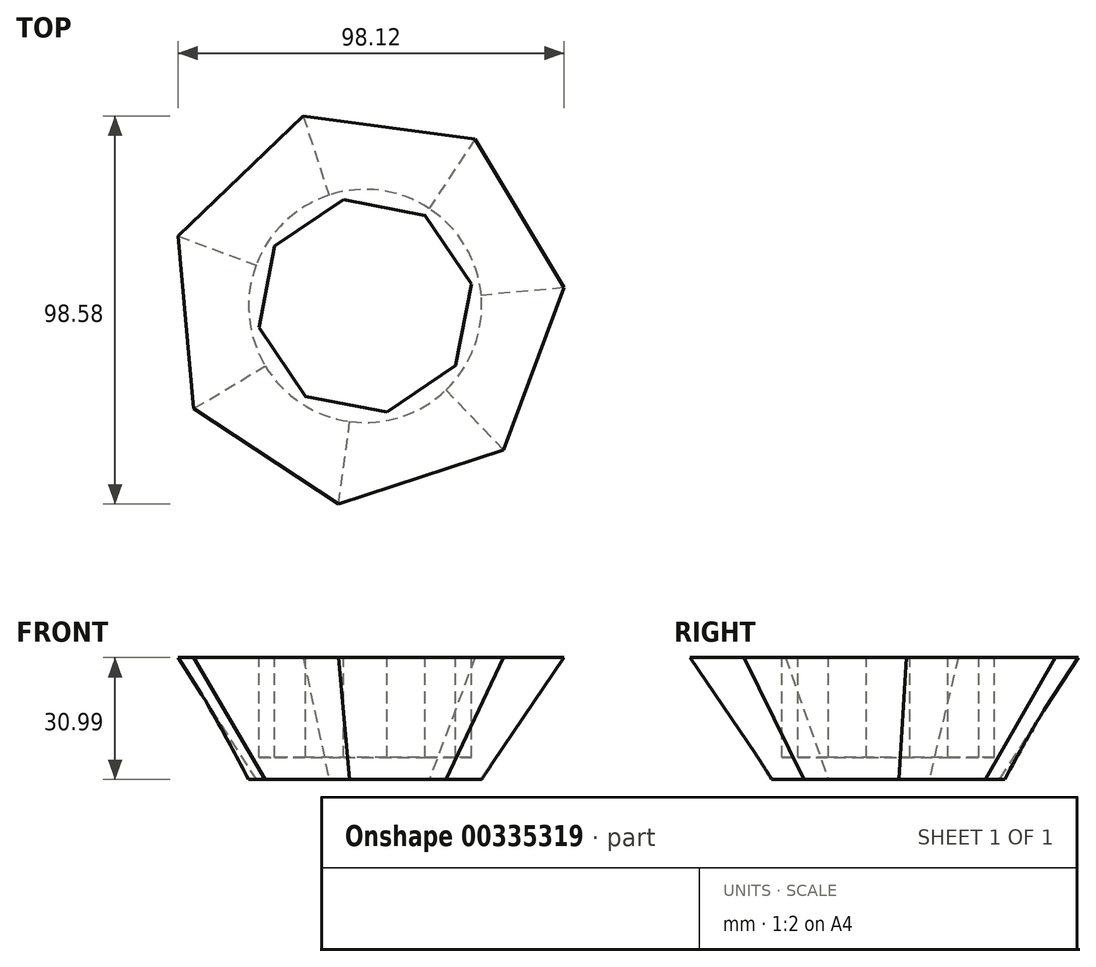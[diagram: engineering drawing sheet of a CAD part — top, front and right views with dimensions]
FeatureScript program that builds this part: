
annotation { "Feature Type Name" : "Feature", "Feature Type Description" : "" }
export const myFeature = defineFeature(function(context is Context, id is Id, definition is map)
    precondition{}
    {
        {
            var Q0;
            Q0=qCreatedBy(makeId("Top.planeOp"),FACE);
            var sketch = newSketch(context, id + "F0", { "sketchPlane" : qUnion([Q0])});
            skCircle(sketch, "E0", {"center": v(0, 0) * mm, "radius": 29.6 * mm});
            skSolve(sketch);
        }
        {
            var Q0;
            Q0=qCreatedBy(makeId("Top.planeOp"),FACE);
            cPlane(context, id + "F1", {"entities" : qUnion([Q0]), "cplaneType" : CPlaneType.OFFSET, "offset" : 30.99 * mm, "width" : 152.4 * mm, "height" : 152.4 * mm});
        }
        {
            var Q0;
            Q0=qCreatedBy(id+"F1.planeOp",FACE);
            var sketch = newSketch(context, id + "F2", { "sketchPlane" : qUnion([Q0])});
            skCircle(sketch, "E1.cCircle", {"center": v(0, 0) * mm, "radius": 45.74 * mm, "construction": true});
            skLineSegment(sketch, "E1.0", {"start": v(27.9, 42.42) * mm, "end": v(50.56, 4.63) * mm});
            skLineSegment(sketch, "E1.1", {"start": v(50.56, 4.63) * mm, "end": v(35.14, -36.64) * mm});
            skLineSegment(sketch, "E1.2", {"start": v(35.14, -36.64) * mm, "end": v(-6.74, -50.32) * mm});
            skLineSegment(sketch, "E1.3", {"start": v(-6.74, -50.32) * mm, "end": v(-43.55, -26.1) * mm});
            skLineSegment(sketch, "E1.4", {"start": v(-43.55, -26.1) * mm, "end": v(-47.56, 17.77) * mm});
            skLineSegment(sketch, "E1.5", {"start": v(-47.56, 17.77) * mm, "end": v(-15.76, 48.26) * mm});
            skLineSegment(sketch, "E1.6", {"start": v(-15.76, 48.26) * mm, "end": v(27.9, 42.42) * mm});
            skPoint(sketch, "E1.0.midPoint", {"position": v(39.23, 23.52) * mm});
            skSolve(sketch);
        }
        {
            var Q0;
            Q0=makeQuery(id+"F2.imprint","IMPRINT",FACE,{"disambiguationData":[TD([[makeQuery(id+"F2.imprint","IMPRINT",EDGE,{"derivedFrom":sQuery(id+"F2.wireOp",EDGE,"E1.0")}),-1.0]])]});
            var Q1;
            Q1=makeQuery(id+"F0.imprint","IMPRINT",FACE,{"disambiguationData":[TD([[makeQuery(id+"F0.imprint","IMPRINT",EDGE,{"derivedFrom":sQuery(id+"F0.wireOp",EDGE,"E0")}),1.0]])]});
            loft(context, id + "F3", {"sheetProfilesArray" : [{ "sheetProfileEntities" : qUnion([Q0]) }, { "sheetProfileEntities" : qUnion([Q1]) }]});
        }
        {
            var Q0;
            Q0=makeQuery(id+"F3.opLoft","CAP_FACE",FACE,{"disambiguationData":[OSD([makeQuery(id+"F2.imprint","IMPRINT",FACE,{"disambiguationData":[TD([[makeQuery(id+"F2.imprint","IMPRINT",EDGE,{"derivedFrom":sQuery(id+"F2.wireOp",EDGE,"E1.0")}),-1.0]])]})])],"isStart":true});
            var sketch = newSketch(context, id + "F4", { "sketchPlane" : qUnion([Q0])});
            skCircle(sketch, "E2.cCircle", {"center": v(0, 0) * mm, "radius": 25.44 * mm, "construction": true});
            skLineSegment(sketch, "E2.0", {"start": v(15.16, 22.99) * mm, "end": v(26.98, 5.53) * mm});
            skLineSegment(sketch, "E2.1", {"start": v(26.98, 5.53) * mm, "end": v(22.99, -15.16) * mm});
            skLineSegment(sketch, "E2.2", {"start": v(22.99, -15.16) * mm, "end": v(5.53, -26.98) * mm});
            skLineSegment(sketch, "E2.3", {"start": v(5.53, -26.98) * mm, "end": v(-15.16, -22.99) * mm});
            skLineSegment(sketch, "E2.4", {"start": v(-15.16, -22.99) * mm, "end": v(-26.98, -5.53) * mm});
            skLineSegment(sketch, "E2.5", {"start": v(-26.98, -5.53) * mm, "end": v(-22.99, 15.16) * mm});
            skLineSegment(sketch, "E2.6", {"start": v(-22.99, 15.16) * mm, "end": v(-5.53, 26.98) * mm});
            skLineSegment(sketch, "E2.7", {"start": v(-5.53, 26.98) * mm, "end": v(15.16, 22.99) * mm});
            skPoint(sketch, "E2.0.midPoint", {"position": v(21.07, 14.26) * mm});
            skSolve(sketch);
        }
        {
            var Q0;
            Q0=makeQuery(id+"F4.imprint","IMPRINT",FACE,{"disambiguationData":[TD([[makeQuery(id+"F4.imprint","IMPRINT",EDGE,{"derivedFrom":sQuery(id+"F4.wireOp",EDGE,"E2.0")}),-1.0]])]});
            extrude(context, id + "F5", {"entities" : qUnion([Q0]), "operationType" : NewBodyOperationType.REMOVE, "oppositeDirection" : true, "depth" : 25.4 * mm});
        }
    });
